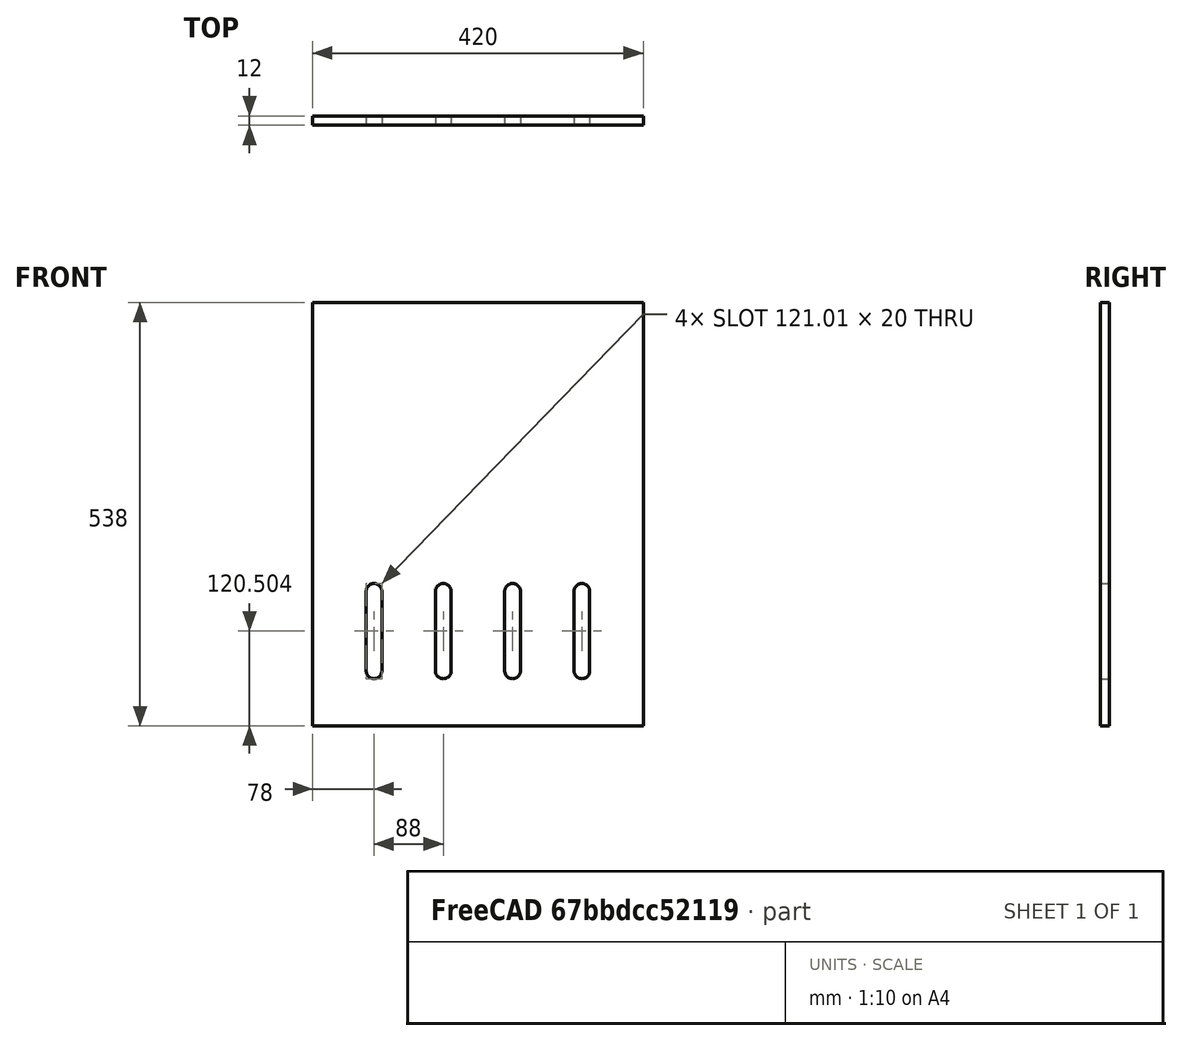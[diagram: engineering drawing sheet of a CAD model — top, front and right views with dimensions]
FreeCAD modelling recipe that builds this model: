
FCSTD DOCUMENT  (FreeCAD 0.18R16131 (Git))
Label: Top_plate
License: All rights reserved
LicenseURL: http://en.wikipedia.org/wiki/All_rights_reserved
objects: Sketcher::SketchObject×1, PartDesign::Pad×1, PartDesign::Body×1
note: 4 computed .brp shape members not serialized (recipe doc carries the construction recipe); baked Part::Feature solids carry a one-line shape summary decoded from their .brp

FEATURE [Sketcher::SketchObject] Sketch
  MapMode = 5
  Placement = pos=(0,0,0) rot=(1,0,0;1.5708rad)
  Support = -> [XZ_Plane]
  sketch-geometry (25):
    g0: LineSegment StartX=0 StartY=0 StartZ=0 EndX=420 EndY=0 EndZ=0
    g1: LineSegment StartX=420 StartY=0 StartZ=0 EndX=420 EndY=-538 EndZ=0
    g2: LineSegment StartX=420 StartY=-538 StartZ=0 EndX=0 EndY=-538 EndZ=0
    g3: LineSegment StartX=0 StartY=-538 StartZ=0 EndX=0 EndY=0 EndZ=0
    g4: ArcOfCircle CenterX=78 CenterY=-366.992 CenterZ=0 NormalX=0 NormalY=0 NormalZ=1 AngleXU=0 Radius=10 StartAngle=-1.8e-15 EndAngle=3.14159
    g5: ArcOfCircle CenterX=78 CenterY=-468 CenterZ=0 NormalX=0 NormalY=0 NormalZ=1 AngleXU=0 Radius=10 StartAngle=3.14159 EndAngle=6.28319
    g6: LineSegment StartX=68 StartY=-366.992 StartZ=0 EndX=68 EndY=-468 EndZ=0
    g7: LineSegment StartX=88 StartY=-366.992 StartZ=0 EndX=88 EndY=-468 EndZ=0
    g8: ArcOfCircle CenterX=254 CenterY=-366.992 CenterZ=0 NormalX=0 NormalY=0 NormalZ=1 AngleXU=0 Radius=10 StartAngle=-1.8e-15 EndAngle=3.14159
    g9: ArcOfCircle CenterX=254 CenterY=-468 CenterZ=0 NormalX=0 NormalY=0 NormalZ=1 AngleXU=0 Radius=10 StartAngle=3.14159 EndAngle=6.28319
    g10: LineSegment StartX=244 StartY=-366.992 StartZ=0 EndX=244 EndY=-468 EndZ=0
    g11: LineSegment StartX=264 StartY=-366.992 StartZ=0 EndX=264 EndY=-468 EndZ=0
    g12: ArcOfCircle CenterX=342 CenterY=-366.992 CenterZ=0 NormalX=0 NormalY=0 NormalZ=1 AngleXU=0 Radius=10 StartAngle=-1.8e-15 EndAngle=3.14159
    g13: ArcOfCircle CenterX=342 CenterY=-468 CenterZ=0 NormalX=0 NormalY=0 NormalZ=1 AngleXU=0 Radius=10 StartAngle=3.14159 EndAngle=6.28319
    g14: LineSegment StartX=332 StartY=-366.992 StartZ=0 EndX=332 EndY=-468 EndZ=0
    g15: LineSegment StartX=352 StartY=-366.992 StartZ=0 EndX=352 EndY=-468 EndZ=0
    g16: ArcOfCircle CenterX=166 CenterY=-366.992 CenterZ=0 NormalX=0 NormalY=0 NormalZ=1 AngleXU=0 Radius=10 StartAngle=-1.8e-15 EndAngle=3.14159
    g17: ArcOfCircle CenterX=166 CenterY=-468 CenterZ=0 NormalX=0 NormalY=0 NormalZ=1 AngleXU=0 Radius=10 StartAngle=3.14159 EndAngle=6.28319
    g18: LineSegment StartX=156 StartY=-366.992 StartZ=0 EndX=156 EndY=-468 EndZ=0
    g19: LineSegment StartX=176 StartY=-366.992 StartZ=0 EndX=176 EndY=-468 EndZ=0
    g20: LineSegment [constr] StartX=68 StartY=-366.992 StartZ=0 EndX=0 EndY=-366.992 EndZ=0
    g21: LineSegment [constr] StartX=88 StartY=-366.992 StartZ=0 EndX=156 EndY=-366.992 EndZ=0
    g22: LineSegment [constr] StartX=176 StartY=-366.992 StartZ=0 EndX=244 EndY=-366.992 EndZ=0
    g23: LineSegment [constr] StartX=264 StartY=-366.992 StartZ=0 EndX=332 EndY=-366.992 EndZ=0
    g24: LineSegment [constr] StartX=352 StartY=-366.992 StartZ=0 EndX=420 EndY=-366.992 EndZ=0
  constraints (62):
    c: Coincident(g0,g1)
    c: Coincident(g1,g2)
    c: Coincident(g2,g3)
    c: Coincident(g3,g0)
    c: Horizontal(g0)
    c: Horizontal(g2)
    c: Vertical(g1)
    c: Vertical(g3)
    c: Coincident(g0,g-1)
    c: DistanceX(g0,g0) = 420
    c: DistanceY(g3,g3) = 538
    c: Tangent(g4,g7) = 1.5708
    c: Tangent(g4,g6) = -1.5708
    c: Tangent(g6,g5) = -1.5708
    c: Tangent(g7,g5) = 1.5708
    c: Vertical(g6)
    c: Equal(g4,g5)
    c: Tangent(g8,g11) = 1.5708
    c: Tangent(g8,g10) = -1.5708
    c: Tangent(g10,g9) = -1.5708
    c: Tangent(g11,g9) = 1.5708
    c: Vertical(g10)
    c: Equal(g8,g9)
    c: Tangent(g12,g15) = 1.5708
    c: Tangent(g12,g14) = -1.5708
    c: Tangent(g14,g13) = -1.5708
    c: Tangent(g15,g13) = 1.5708
    c: Vertical(g14)
    c: Equal(g12,g13)
    c: Tangent(g16,g19) = 1.5708
    c: Tangent(g16,g18) = -1.5708
    c: Tangent(g18,g17) = -1.5708
    c: Tangent(g19,g17) = 1.5708
    c: Vertical(g18)
    c: Equal(g16,g17)
    c: Coincident(g20,g4)
    c: PointOnObject(g20,g3)
    c: Horizontal(g20)
    c: Coincident(g21,g4)
    c: Coincident(g21,g16)
    c: Horizontal(g21)
    c: Coincident(g22,g16)
    c: Coincident(g22,g8)
    c: Coincident(g23,g8)
    c: Coincident(g23,g12)
    c: Coincident(g24,g12)
    c: PointOnObject(g24,g1)
    c: Horizontal(g24)
    c: Horizontal(g23)
    c: Horizontal(g22)
    c: Equal(g20,g21)
    c: Equal(g21,g22)
    c: Equal(g22,g23)
    c: Equal(g23,g24)
    c: Equal(g12,g8)
    c: Equal(g8,g16)
    c: Equal(g16,g4)
    c: Equal(g15,g11)
    c: Equal(g11,g19)
    c: Equal(g19,g7)
    c: DistanceY(g2,g5) = 70
    c: Radius(g4) = 10
FEATURE [PartDesign::Pad] Pad
  Length = 12
  Length2 = 100
  Placement = pos=(0,0,0) rot=(1,0,0;1.5708rad)
  Profile = -> Sketch
  Type = 0
FEATURE [PartDesign::Body] Body
  Group = -> [Sketch,Pad]
  Origin = -> Origin
  Tip = -> Pad
